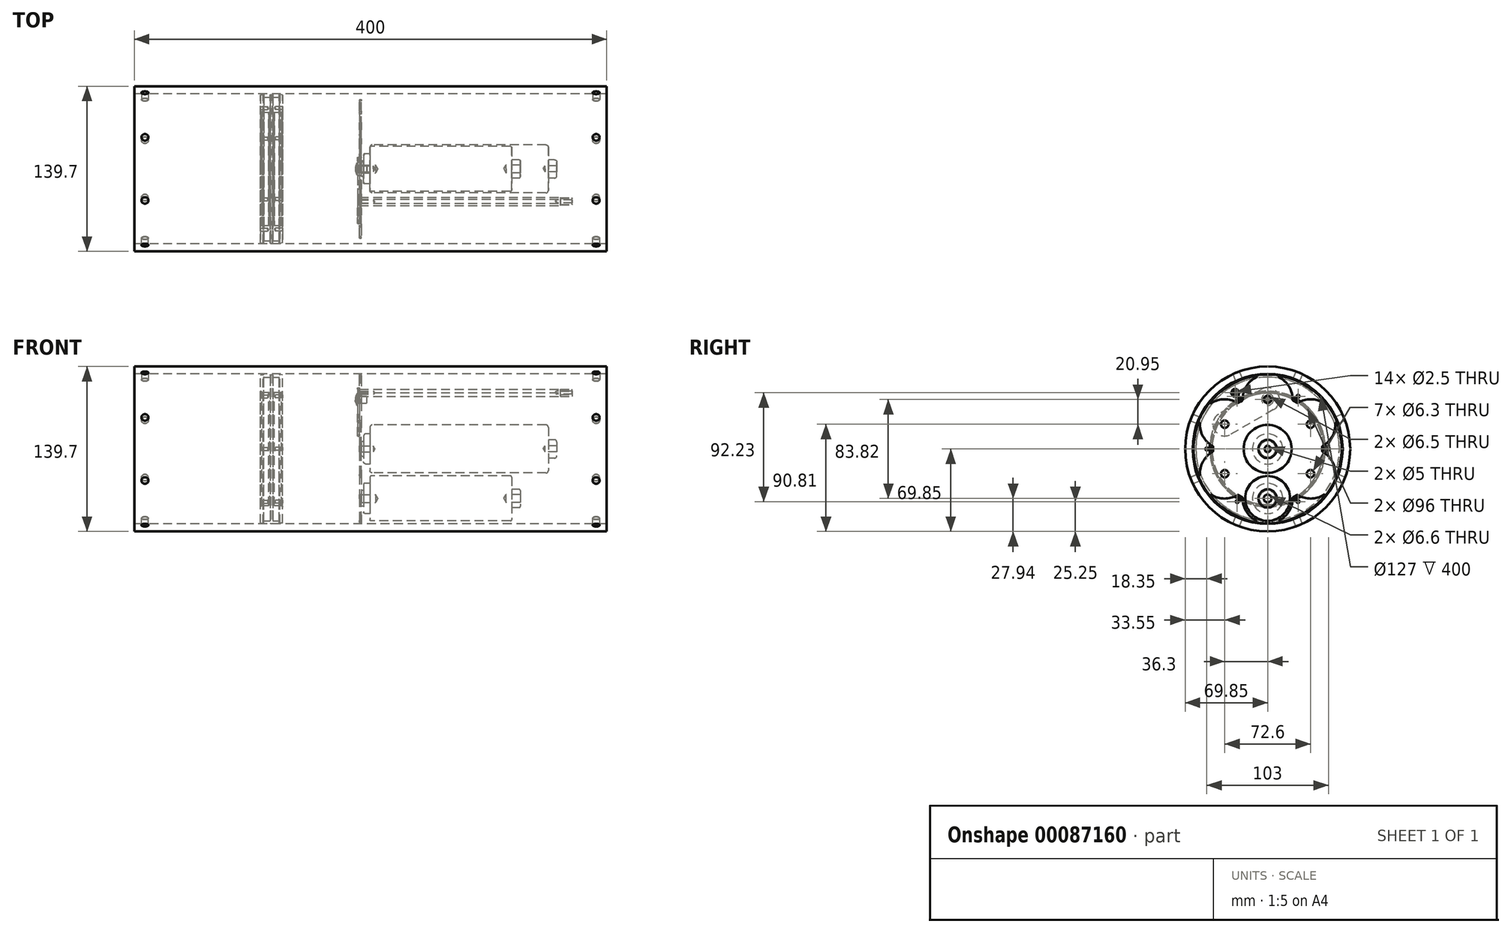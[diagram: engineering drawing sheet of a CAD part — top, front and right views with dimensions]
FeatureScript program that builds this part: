
annotation { "Feature Type Name" : "Feature", "Feature Type Description" : "" }
export const myFeature = defineFeature(function(context is Context, id is Id, definition is map)
    precondition{}
    {
        {
            var Q0;
            Q0=qCreatedBy(makeId("Front.planeOp"),FACE);
            var sketch = newSketch(context, id + "F0", { "sketchPlane" : qUnion([Q0])});
            skLineSegment(sketch, "E0", {"start": v(-82.75, 0) * mm, "end": v(82.75, 0) * mm});
            skLineSegment(sketch, "E1", {"start": v(-75.5, 20.32) * mm, "end": v(75.5, 20.32) * mm});
            skLineSegment(sketch, "E2", {"start": v(-82.75, 0) * mm, "end": v(-82.75, 6.75) * mm});
            skLineSegment(sketch, "E3", {"start": v(-82.75, 6.75) * mm, "end": v(-80.88, 6.75) * mm});
            skLineSegment(sketch, "E4", {"start": v(-80.88, 6.75) * mm, "end": v(-80.88, 12.8) * mm});
            skLineSegment(sketch, "E5", {"start": v(-80.88, 12.8) * mm, "end": v(-75.5, 12.8) * mm});
            skLineSegment(sketch, "E6", {"start": v(-75.5, 12.8) * mm, "end": v(-75.5, 20.32) * mm});
            skLineSegment(sketch, "E7", {"start": v(82.75, 0) * mm, "end": v(82.75, 7.75) * mm});
            skLineSegment(sketch, "E8", {"start": v(82.75, 7.75) * mm, "end": v(75.5, 7.75) * mm});
            skLineSegment(sketch, "E9", {"start": v(75.5, 7.75) * mm, "end": v(75.5, 20.32) * mm});
            skSolve(sketch);
        }
        {
            var Q0;
            Q0=makeQuery(id+"F0.imprint","IMPRINT",FACE,{"disambiguationData":[TD([[makeQuery(id+"F0.imprint","IMPRINT",EDGE,{"derivedFrom":sQuery(id+"F0.wireOp",EDGE,"E0")}),1.0]])]});
            var Q1;
            Q1=sQuery(id+"F0.wireOp",EDGE,"E0");
            revolve(context, id + "F1", {"entities" : qUnion([Q0]), "axis" : qUnion([Q1]), "revolveType" : RevolveType.FULL});
        }
        {
            var Q0;
            Q0=makeQuery(id+"F1.opRevolve","SWEPT_FACE",FACE,{"disambiguationData":[OSD([sQuery(id+"F0.wireOp",EDGE,"E1")])]});
            var Q1;
            Q1=makeQuery(id+"F1.opRevolve","SWEPT_EDGE",EDGE,{"disambiguationData":[OSD([sQuery(id+"F0.wireOp",EDGE,"E7"),sQuery(id+"F0.wireOp",EDGE,"E8")])]});
            var Q2;
            Q2=makeQuery(id+"F1.opRevolve","SWEPT_EDGE",EDGE,{"disambiguationData":[OSD([sQuery(id+"F0.wireOp",EDGE,"E4"),sQuery(id+"F0.wireOp",EDGE,"E5")])]});
            var Q3;
            Q3=makeQuery(id+"F1.opRevolve","SWEPT_EDGE",EDGE,{"disambiguationData":[OSD([sQuery(id+"F0.wireOp",EDGE,"E2"),sQuery(id+"F0.wireOp",EDGE,"E3")])]});
            fillet(context, id + "F2", {"entities" : qUnion([Q0, Q1, Q2, Q3]), "radius" : 2 * mm, "tangentPropagation" : true, "allowEdgeOverflow" : false});
        }
        {
            var Q0;
            Q0=makeQuery(id+"F1.opRevolve","SWEPT_FACE",FACE,{"disambiguationData":[OSD([sQuery(id+"F0.wireOp",EDGE,"E2")])]});
            var sketch = newSketch(context, id + "F3", { "sketchPlane" : qUnion([Q0])});
            skPoint(sketch, "E10", {"position": v(0, 0) * mm});
            skSolve(sketch);
        }
        {
            var Q0;
            Q0=makeQuery(id+"F1.opRevolve","SWEPT_FACE",FACE,{"disambiguationData":[OSD([sQuery(id+"F0.wireOp",EDGE,"E7")])]});
            var sketch = newSketch(context, id + "F4", { "sketchPlane" : qUnion([Q0])});
            skPoint(sketch, "E11", {"position": v(0, 0) * mm});
            skSolve(sketch);
        }
        {
            var Q0;
            Q0=sQuery(id+"F4.wireOp",VERTEX,"E11");
            var Q1;
            Q1=sQuery(id+"F3.wireOp",VERTEX,"E10");
            var Q2;
            Q2=makeQuery(id+"F1.opRevolve","SWEPT_BODY",BODY,{"disambiguationData":[OSD([sQuery(id+"F0.wireOp",EDGE,"E0"),sQuery(id+"F0.wireOp",EDGE,"E1"),sQuery(id+"F0.wireOp",EDGE,"E2"),sQuery(id+"F0.wireOp",EDGE,"E3"),sQuery(id+"F0.wireOp",EDGE,"E4"),sQuery(id+"F0.wireOp",EDGE,"E5"),sQuery(id+"F0.wireOp",EDGE,"E6"),sQuery(id+"F0.wireOp",EDGE,"E7"),sQuery(id+"F0.wireOp",EDGE,"E8"),sQuery(id+"F0.wireOp",EDGE,"E9")])]});
            hole(context, id + "F5", {"style" : HoleStyle.SIMPLE, "endStyle" : HoleEndStyle.BLIND, "standardTappedOrClearance" : lookupTablePath({ "standard" : "ISO", "engagement" : "75%", "pitch" : "1 mm", "size" : "M6", "type" : "Tapped" }), "standardBlindInLast" : lookupTablePath({ "standard" : "ISO", "engagement" : "75%", "pitch" : "1 mm", "size" : "M6", "type" : "Tapped" }), "holeDiameter" : 5 * mm, "holeDepth" : 10 * mm, "locations" : qUnion([Q0, Q1]), "scope" : qUnion([Q2]), "majorDiameter" : 6 * mm});
        }
        {
            var Q0;
            Q0=makeQuery(id+"F1.opRevolve","SWEPT_FACE",FACE,{"disambiguationData":[OSD([sQuery(id+"F0.wireOp",EDGE,"E2")])]});
            var sketch = newSketch(context, id + "F6", { "sketchPlane" : qUnion([Q0])});
            skCircle(sketch, "E12", {"center": v(0, 0) * mm, "radius": 63.5 * mm, "construction": true});
            skCircle(sketch, "E13.0", {"center": v(0, 0) * mm, "radius": 20.32 * mm, "construction": true});
            skLineSegment(sketch, "E14", {"start": v(0, 20.32) * mm, "end": v(0, 63.5) * mm, "construction": true});
            skCircle(sketch, "E15", {"center": v(0, 41.91) * mm, "radius": 20.32 * mm, "construction": true});
            skCircle(sketch, "E16", {"center": v(0, 41.91) * mm, "radius": 3.15 * mm});
            skCircle(sketch, "E17", {"center": v(0, 0) * mm, "radius": 3.15 * mm});
            skCircle(sketch, "E18", {"center": v(0, 0) * mm, "radius": 63 * mm});
            skCircle(sketch, "E19.1.0", {"center": v(-36.3, 20.96) * mm, "radius": 3.15 * mm});
            skCircle(sketch, "E19.2.0", {"center": v(-36.3, -20.96) * mm, "radius": 3.15 * mm});
            skCircle(sketch, "E19.3.0", {"center": v(0, -41.91) * mm, "radius": 3.15 * mm});
            skCircle(sketch, "E19.4.0", {"center": v(36.3, -20.96) * mm, "radius": 3.15 * mm});
            skCircle(sketch, "E19.5.0", {"center": v(36.3, 20.96) * mm, "radius": 3.15 * mm});
            skCircle(sketch, "E20", {"center": v(36.3, 20.96) * mm, "radius": 20.32 * mm, "construction": true});
            skCircle(sketch, "E21", {"center": v(0, 41.91) * mm, "radius": 10 * mm, "construction": true});
            skCircle(sketch, "E22", {"center": v(36.3, 20.96) * mm, "radius": 10 * mm, "construction": true});
            skLineSegment(sketch, "E23", {"start": v(-5, 33.25) * mm, "end": v(31.3, 12.3) * mm, "construction": true});
            skLineSegment(sketch, "E24", {"start": v(5, 50.57) * mm, "end": v(41.3, 29.62) * mm, "construction": true});
            skArc(sketch, "E25", {"start": v(0, 63) * mm, "mid": v(15.13, 56.6) * mm, "end": v(21.08, 41.29) * mm});
            skLineSegment(sketch, "E26", {"start": v(23.15, 40.1) * mm, "end": v(35.3, 61.15) * mm, "construction": true});
            skArc(sketch, "E27.MirrorCS", {"start": v(54.56, 31.5) * mm, "mid": v(41.45, 41.4) * mm, "end": v(25.22, 38.9) * mm});
            skLineSegment(sketch, "E28", {"start": v(21.08, 41.29) * mm, "end": v(25.22, 38.9) * mm});
            skLineSegment(sketch, "E29", {"start": v(9.66, 62.25) * mm, "end": v(9.43, 60.77) * mm});
            skCircle(sketch, "E30", {"center": v(0, -41.91) * mm, "radius": 19 * mm, "construction": true});
            skCircle(sketch, "E31", {"center": v(-36.3, -20.96) * mm, "radius": 19 * mm, "construction": true});
            skSolve(sketch);
        }
        {
            var Q0;
            Q0 = qSketchRegion(id + "F6", true);
            extrude(context, id + "F7", {"entities" : qUnion([Q0]), "depth" : 1.6 * mm});
        }
        {
            var Q0;
            Q0=makeQuery(id+"F7.opExtrude","CAP_FACE",FACE,{"disambiguationData":[OSD([sQuery(id+"F6.wireOp",EDGE,"E16"),sQuery(id+"F6.wireOp",EDGE,"E17"),sQuery(id+"F6.wireOp",EDGE,"E18"),sQuery(id+"F6.wireOp",EDGE,"E19.1.0"),sQuery(id+"F6.wireOp",EDGE,"E19.2.0"),sQuery(id+"F6.wireOp",EDGE,"E19.3.0"),sQuery(id+"F6.wireOp",EDGE,"E19.4.0"),sQuery(id+"F6.wireOp",EDGE,"E19.5.0")])],"isStart":false});
            var sketch = newSketch(context, id + "F8", { "sketchPlane" : qUnion([Q0])});
            skArc(sketch, "E32.0", {"start": v(9.94, 60.51) * mm, "mid": v(18.13, 52.69) * mm, "end": v(21.09, 41.75) * mm});
            skArc(sketch, "E32.1", {"start": v(47.44, 38.86) * mm, "mid": v(36.57, 42.04) * mm, "end": v(25.62, 39.14) * mm});
            skArc(sketch, "E32.2", {"start": v(49.08, 39.5) * mm, "mid": v(31.5, 54.56) * mm, "end": v(9.66, 62.25) * mm});
            skLineSegment(sketch, "E32.3", {"start": v(9.66, 62.25) * mm, "end": v(9.52, 61.34) * mm});
            skLineSegment(sketch, "E32.4", {"start": v(21.49, 41.05) * mm, "end": v(24.81, 39.14) * mm});
            skLineSegment(sketch, "E32.5", {"start": v(23.15, 40.1) * mm, "end": v(35.3, 61.15) * mm, "construction": true});
            skLineSegment(sketch, "E33.MirrorCS", {"start": v(49.08, 39.5) * mm, "end": v(48.36, 38.92) * mm});
            skPoint(sketch, "E34.orphan", {"position": v(54.56, 31.5) * mm});
            skPoint(sketch, "E35.orphan", {"position": v(0, 63) * mm});
            skPoint(sketch, "E36.visualSharp", {"position": v(21.08, 41.29) * mm});
            skArc(sketch, "E36.filletArc", {"start": v(21.09, 41.75) * mm, "mid": v(21.2, 41.35) * mm, "end": v(21.49, 41.05) * mm});
            skPoint(sketch, "E37.visualSharp", {"position": v(25.22, 38.9) * mm});
            skArc(sketch, "E37.filletArc", {"start": v(24.81, 39.14) * mm, "mid": v(25.21, 39.03) * mm, "end": v(25.62, 39.14) * mm});
            skPoint(sketch, "E38.visualSharp", {"position": v(47.91, 38.56) * mm});
            skArc(sketch, "E38.filletArc", {"start": v(47.44, 38.86) * mm, "mid": v(47.9, 38.74) * mm, "end": v(48.36, 38.92) * mm});
            skPoint(sketch, "E39.visualSharp", {"position": v(9.43, 60.77) * mm});
            skArc(sketch, "E39.filletArc", {"start": v(9.52, 61.34) * mm, "mid": v(9.6, 60.86) * mm, "end": v(9.94, 60.51) * mm});
            skPoint(sketch, "E40.1.1", {"position": v(-54.56, 31.5) * mm});
            skArc(sketch, "E40.1.2", {"start": v(-47.44, 38.86) * mm, "mid": v(-36.57, 42.04) * mm, "end": v(-25.62, 39.14) * mm});
            skArc(sketch, "E40.1.3", {"start": v(-9.94, 60.51) * mm, "mid": v(-18.13, 52.69) * mm, "end": v(-21.09, 41.75) * mm});
            skArc(sketch, "E40.1.4", {"start": v(-9.66, 62.25) * mm, "mid": v(-31.5, 54.56) * mm, "end": v(-49.08, 39.5) * mm});
            skLineSegment(sketch, "E40.1.5", {"start": v(-23.15, 40.1) * mm, "end": v(-35.3, 61.15) * mm, "construction": true});
            skPoint(sketch, "E40.1.6", {"position": v(-25.22, 38.9) * mm});
            skPoint(sketch, "E40.1.7", {"position": v(-21.08, 41.29) * mm});
            skPoint(sketch, "E40.1.8", {"position": v(-9.43, 60.77) * mm});
            skPoint(sketch, "E40.1.9", {"position": v(-47.91, 38.56) * mm});
            skLineSegment(sketch, "E40.1.10", {"start": v(-24.81, 39.14) * mm, "end": v(-21.49, 41.05) * mm});
            skArc(sketch, "E40.1.11", {"start": v(-48.36, 38.92) * mm, "mid": v(-47.9, 38.74) * mm, "end": v(-47.44, 38.86) * mm});
            skLineSegment(sketch, "E40.1.12", {"start": v(-49.08, 39.5) * mm, "end": v(-48.36, 38.92) * mm});
            skArc(sketch, "E40.1.13", {"start": v(-25.62, 39.14) * mm, "mid": v(-25.21, 39.03) * mm, "end": v(-24.81, 39.14) * mm});
            skArc(sketch, "E40.1.14", {"start": v(-21.49, 41.05) * mm, "mid": v(-21.2, 41.35) * mm, "end": v(-21.09, 41.75) * mm});
            skLineSegment(sketch, "E40.1.15", {"start": v(-9.66, 62.25) * mm, "end": v(-9.52, 61.34) * mm});
            skArc(sketch, "E40.1.16", {"start": v(-9.94, 60.51) * mm, "mid": v(-9.6, 60.86) * mm, "end": v(-9.52, 61.34) * mm});
            skPoint(sketch, "E40.2.0", {"position": v(-54.56, 31.5) * mm});
            skPoint(sketch, "E40.2.1", {"position": v(-54.56, -31.5) * mm});
            skArc(sketch, "E40.2.2", {"start": v(-57.37, -21.65) * mm, "mid": v(-54.7, -10.65) * mm, "end": v(-46.7, -2.61) * mm});
            skArc(sketch, "E40.2.3", {"start": v(-57.37, 21.65) * mm, "mid": v(-54.7, 10.65) * mm, "end": v(-46.7, 2.61) * mm});
            skArc(sketch, "E40.2.4", {"start": v(-58.75, 22.76) * mm, "mid": v(-63, 0) * mm, "end": v(-58.75, -22.76) * mm});
            skLineSegment(sketch, "E40.2.5", {"start": v(-46.3, 0) * mm, "end": v(-70.6, 0) * mm, "construction": true});
            skPoint(sketch, "E40.2.6", {"position": v(-46.3, -2.4) * mm});
            skPoint(sketch, "E40.2.7", {"position": v(-46.3, 2.4) * mm});
            skPoint(sketch, "E40.2.8", {"position": v(-57.35, 22.22) * mm});
            skPoint(sketch, "E40.2.9", {"position": v(-57.35, -22.22) * mm});
            skLineSegment(sketch, "E40.2.10", {"start": v(-46.3, -1.92) * mm, "end": v(-46.3, 1.92) * mm});
            skArc(sketch, "E40.2.11", {"start": v(-57.88, -22.42) * mm, "mid": v(-57.5, -22.12) * mm, "end": v(-57.37, -21.65) * mm});
            skLineSegment(sketch, "E40.2.12", {"start": v(-58.75, -22.76) * mm, "end": v(-57.88, -22.42) * mm});
            skArc(sketch, "E40.2.13", {"start": v(-46.7, -2.61) * mm, "mid": v(-46.4, -2.32) * mm, "end": v(-46.3, -1.92) * mm});
            skArc(sketch, "E40.2.14", {"start": v(-46.3, 1.92) * mm, "mid": v(-46.4, 2.32) * mm, "end": v(-46.7, 2.61) * mm});
            skLineSegment(sketch, "E40.2.15", {"start": v(-58.75, 22.76) * mm, "end": v(-57.88, 22.42) * mm});
            skArc(sketch, "E40.2.16", {"start": v(-57.37, 21.65) * mm, "mid": v(-57.5, 22.12) * mm, "end": v(-57.88, 22.42) * mm});
            skPoint(sketch, "E40.3.0", {"position": v(-54.56, -31.5) * mm});
            skPoint(sketch, "E40.3.1", {"position": v(0, -63) * mm});
            skArc(sketch, "E40.3.2", {"start": v(-9.94, -60.51) * mm, "mid": v(-18.13, -52.69) * mm, "end": v(-21.09, -41.75) * mm});
            skArc(sketch, "E40.3.3", {"start": v(-47.44, -38.86) * mm, "mid": v(-36.57, -42.04) * mm, "end": v(-25.62, -39.14) * mm});
            skArc(sketch, "E40.3.4", {"start": v(-49.08, -39.5) * mm, "mid": v(-31.5, -54.56) * mm, "end": v(-9.66, -62.25) * mm});
            skLineSegment(sketch, "E40.3.5", {"start": v(-23.15, -40.1) * mm, "end": v(-35.3, -61.15) * mm, "construction": true});
            skPoint(sketch, "E40.3.6", {"position": v(-21.08, -41.29) * mm});
            skPoint(sketch, "E40.3.7", {"position": v(-25.22, -38.9) * mm});
            skPoint(sketch, "E40.3.8", {"position": v(-47.91, -38.56) * mm});
            skPoint(sketch, "E40.3.9", {"position": v(-9.43, -60.77) * mm});
            skLineSegment(sketch, "E40.3.10", {"start": v(-21.49, -41.05) * mm, "end": v(-24.81, -39.14) * mm});
            skArc(sketch, "E40.3.11", {"start": v(-9.52, -61.34) * mm, "mid": v(-9.6, -60.86) * mm, "end": v(-9.94, -60.51) * mm});
            skLineSegment(sketch, "E40.3.12", {"start": v(-9.66, -62.25) * mm, "end": v(-9.52, -61.34) * mm});
            skArc(sketch, "E40.3.13", {"start": v(-21.09, -41.75) * mm, "mid": v(-21.2, -41.35) * mm, "end": v(-21.49, -41.05) * mm});
            skArc(sketch, "E40.3.14", {"start": v(-24.81, -39.14) * mm, "mid": v(-25.21, -39.03) * mm, "end": v(-25.62, -39.14) * mm});
            skLineSegment(sketch, "E40.3.15", {"start": v(-49.08, -39.5) * mm, "end": v(-48.36, -38.92) * mm});
            skArc(sketch, "E40.3.16", {"start": v(-47.44, -38.86) * mm, "mid": v(-47.9, -38.74) * mm, "end": v(-48.36, -38.92) * mm});
            skPoint(sketch, "E40.4.0", {"position": v(0, -63) * mm});
            skPoint(sketch, "E40.4.1", {"position": v(54.56, -31.5) * mm});
            skArc(sketch, "E40.4.2", {"start": v(47.44, -38.86) * mm, "mid": v(36.57, -42.04) * mm, "end": v(25.62, -39.14) * mm});
            skArc(sketch, "E40.4.3", {"start": v(9.94, -60.51) * mm, "mid": v(18.13, -52.69) * mm, "end": v(21.09, -41.75) * mm});
            skArc(sketch, "E40.4.4", {"start": v(9.66, -62.25) * mm, "mid": v(31.5, -54.56) * mm, "end": v(49.08, -39.5) * mm});
            skLineSegment(sketch, "E40.4.5", {"start": v(23.15, -40.1) * mm, "end": v(35.3, -61.15) * mm, "construction": true});
            skPoint(sketch, "E40.4.6", {"position": v(25.22, -38.9) * mm});
            skPoint(sketch, "E40.4.7", {"position": v(21.08, -41.29) * mm});
            skPoint(sketch, "E40.4.8", {"position": v(9.43, -60.77) * mm});
            skPoint(sketch, "E40.4.9", {"position": v(47.91, -38.56) * mm});
            skLineSegment(sketch, "E40.4.10", {"start": v(24.81, -39.14) * mm, "end": v(21.49, -41.05) * mm});
            skArc(sketch, "E40.4.11", {"start": v(48.36, -38.92) * mm, "mid": v(47.9, -38.74) * mm, "end": v(47.44, -38.86) * mm});
            skLineSegment(sketch, "E40.4.12", {"start": v(49.08, -39.5) * mm, "end": v(48.36, -38.92) * mm});
            skArc(sketch, "E40.4.13", {"start": v(25.62, -39.14) * mm, "mid": v(25.21, -39.03) * mm, "end": v(24.81, -39.14) * mm});
            skArc(sketch, "E40.4.14", {"start": v(21.49, -41.05) * mm, "mid": v(21.2, -41.35) * mm, "end": v(21.09, -41.75) * mm});
            skLineSegment(sketch, "E40.4.15", {"start": v(9.66, -62.25) * mm, "end": v(9.52, -61.34) * mm});
            skArc(sketch, "E40.4.16", {"start": v(9.94, -60.51) * mm, "mid": v(9.6, -60.86) * mm, "end": v(9.52, -61.34) * mm});
            skPoint(sketch, "E40.5.0", {"position": v(54.56, -31.5) * mm});
            skArc(sketch, "E40.5.2", {"start": v(57.37, 21.65) * mm, "mid": v(54.7, 10.65) * mm, "end": v(46.7, 2.61) * mm});
            skArc(sketch, "E40.5.3", {"start": v(57.37, -21.65) * mm, "mid": v(54.7, -10.65) * mm, "end": v(46.7, -2.61) * mm});
            skArc(sketch, "E40.5.4", {"start": v(58.75, -22.76) * mm, "mid": v(63, 0) * mm, "end": v(58.75, 22.76) * mm});
            skLineSegment(sketch, "E40.5.5", {"start": v(46.3, 0) * mm, "end": v(70.6, 0) * mm, "construction": true});
            skPoint(sketch, "E40.5.6", {"position": v(46.3, 2.4) * mm});
            skPoint(sketch, "E40.5.7", {"position": v(46.3, -2.4) * mm});
            skPoint(sketch, "E40.5.8", {"position": v(57.35, -22.22) * mm});
            skPoint(sketch, "E40.5.9", {"position": v(57.35, 22.22) * mm});
            skLineSegment(sketch, "E40.5.10", {"start": v(46.3, 1.92) * mm, "end": v(46.3, -1.92) * mm});
            skArc(sketch, "E40.5.11", {"start": v(57.88, 22.42) * mm, "mid": v(57.5, 22.12) * mm, "end": v(57.37, 21.65) * mm});
            skLineSegment(sketch, "E40.5.12", {"start": v(58.75, 22.76) * mm, "end": v(57.88, 22.42) * mm});
            skArc(sketch, "E40.5.13", {"start": v(46.7, 2.61) * mm, "mid": v(46.4, 2.32) * mm, "end": v(46.3, 1.92) * mm});
            skArc(sketch, "E40.5.14", {"start": v(46.3, -1.92) * mm, "mid": v(46.4, -2.32) * mm, "end": v(46.7, -2.61) * mm});
            skLineSegment(sketch, "E40.5.15", {"start": v(58.75, -22.76) * mm, "end": v(57.88, -22.42) * mm});
            skArc(sketch, "E40.5.16", {"start": v(57.37, -21.65) * mm, "mid": v(57.5, -22.12) * mm, "end": v(57.88, -22.42) * mm});
            skSolve(sketch);
        }
        {
            var Q0;
            Q0 = qSketchRegion(id + "F8", true);
            extrude(context, id + "F9", {"entities" : qUnion([Q0]), "operationType" : NewBodyOperationType.REMOVE, "oppositeDirection" : true, "depth" : 25 * mm});
        }
        {
            var Q0;
            Q0=makeQuery(id+"F9.boolean.opBoolean","COPY",EDGE,{"derivedFrom":makeQuery(id+"F9.opExtrude","SWEPT_EDGE",EDGE,{"disambiguationData":[OSD([sQuery(id+"F6.wireOp",EDGE,"E18"),sQuery(id+"F8.wireOp",EDGE,"E32.2"),sQuery(id+"F8.wireOp",EDGE,"E32.3")])]})});
            var Q1;
            Q1=makeQuery(id+"F9.boolean.opBoolean","COPY",EDGE,{"derivedFrom":makeQuery(id+"F9.opExtrude","SWEPT_EDGE",EDGE,{"disambiguationData":[OSD([sQuery(id+"F6.wireOp",EDGE,"E18"),sQuery(id+"F8.wireOp",EDGE,"E32.2"),sQuery(id+"F8.wireOp",EDGE,"E33.MirrorCS")])]})});
            var Q2;
            Q2=makeQuery(id+"FGbRxVnL68Y7Bjd_2.1.F9.boolean.opBoolean","COPY",EDGE,{"derivedFrom":makeQuery(id+"FGbRxVnL68Y7Bjd_2.1.F9.opExtrude","SWEPT_EDGE",EDGE,{"disambiguationData":[OSD([sQuery(id+"F6.wireOp",EDGE,"E18"),sQuery(id+"F8.wireOp",EDGE,"E32.2"),sQuery(id+"F8.wireOp",EDGE,"E32.3")])]})});
            var Q3;
            Q3=makeQuery(id+"FGbRxVnL68Y7Bjd_2.1.F9.boolean.opBoolean","COPY",EDGE,{"derivedFrom":makeQuery(id+"FGbRxVnL68Y7Bjd_2.1.F9.opExtrude","SWEPT_EDGE",EDGE,{"disambiguationData":[OSD([sQuery(id+"F6.wireOp",EDGE,"E18"),sQuery(id+"F8.wireOp",EDGE,"E32.2"),sQuery(id+"F8.wireOp",EDGE,"E33.MirrorCS")])]})});
            var Q4;
            Q4=makeQuery(id+"FGbRxVnL68Y7Bjd_2.2.F9.boolean.opBoolean","COPY",EDGE,{"derivedFrom":makeQuery(id+"FGbRxVnL68Y7Bjd_2.2.F9.opExtrude","SWEPT_EDGE",EDGE,{"disambiguationData":[OSD([sQuery(id+"F6.wireOp",EDGE,"E18"),sQuery(id+"F8.wireOp",EDGE,"E32.2"),sQuery(id+"F8.wireOp",EDGE,"E32.3")])]})});
            var Q5;
            Q5=makeQuery(id+"FGbRxVnL68Y7Bjd_2.2.F9.boolean.opBoolean","COPY",EDGE,{"derivedFrom":makeQuery(id+"FGbRxVnL68Y7Bjd_2.2.F9.opExtrude","SWEPT_EDGE",EDGE,{"disambiguationData":[OSD([sQuery(id+"F6.wireOp",EDGE,"E18"),sQuery(id+"F8.wireOp",EDGE,"E32.2"),sQuery(id+"F8.wireOp",EDGE,"E33.MirrorCS")])]})});
            var Q6;
            Q6=makeQuery(id+"FGbRxVnL68Y7Bjd_2.3.F9.boolean.opBoolean","COPY",EDGE,{"derivedFrom":makeQuery(id+"FGbRxVnL68Y7Bjd_2.3.F9.opExtrude","SWEPT_EDGE",EDGE,{"disambiguationData":[OSD([sQuery(id+"F6.wireOp",EDGE,"E18"),sQuery(id+"F8.wireOp",EDGE,"E32.2"),sQuery(id+"F8.wireOp",EDGE,"E32.3")])]})});
            var Q7;
            Q7=makeQuery(id+"FGbRxVnL68Y7Bjd_2.4.F9.boolean.opBoolean","COPY",EDGE,{"derivedFrom":makeQuery(id+"FGbRxVnL68Y7Bjd_2.4.F9.opExtrude","SWEPT_EDGE",EDGE,{"disambiguationData":[OSD([sQuery(id+"F6.wireOp",EDGE,"E18"),sQuery(id+"F8.wireOp",EDGE,"E32.2"),sQuery(id+"F8.wireOp",EDGE,"E32.3")])]})});
            var Q8;
            Q8=makeQuery(id+"FGbRxVnL68Y7Bjd_2.3.F9.boolean.opBoolean","COPY",EDGE,{"derivedFrom":makeQuery(id+"FGbRxVnL68Y7Bjd_2.3.F9.opExtrude","SWEPT_EDGE",EDGE,{"disambiguationData":[OSD([sQuery(id+"F6.wireOp",EDGE,"E18"),sQuery(id+"F8.wireOp",EDGE,"E32.2"),sQuery(id+"F8.wireOp",EDGE,"E33.MirrorCS")])]})});
            var Q9;
            Q9=makeQuery(id+"FGbRxVnL68Y7Bjd_2.4.F9.boolean.opBoolean","COPY",EDGE,{"derivedFrom":makeQuery(id+"FGbRxVnL68Y7Bjd_2.4.F9.opExtrude","SWEPT_EDGE",EDGE,{"disambiguationData":[OSD([sQuery(id+"F6.wireOp",EDGE,"E18"),sQuery(id+"F8.wireOp",EDGE,"E32.2"),sQuery(id+"F8.wireOp",EDGE,"E33.MirrorCS")])]})});
            var Q10;
            Q10=makeQuery(id+"FGbRxVnL68Y7Bjd_2.5.F9.boolean.opBoolean","COPY",EDGE,{"derivedFrom":makeQuery(id+"FGbRxVnL68Y7Bjd_2.5.F9.opExtrude","SWEPT_EDGE",EDGE,{"disambiguationData":[OSD([sQuery(id+"F6.wireOp",EDGE,"E18"),sQuery(id+"F8.wireOp",EDGE,"E32.2"),sQuery(id+"F8.wireOp",EDGE,"E32.3")])]})});
            var Q11;
            Q11=makeQuery(id+"FGbRxVnL68Y7Bjd_2.5.F9.boolean.opBoolean","COPY",EDGE,{"derivedFrom":makeQuery(id+"FGbRxVnL68Y7Bjd_2.5.F9.opExtrude","SWEPT_EDGE",EDGE,{"disambiguationData":[OSD([sQuery(id+"F6.wireOp",EDGE,"E18"),sQuery(id+"F8.wireOp",EDGE,"E32.2"),sQuery(id+"F8.wireOp",EDGE,"E33.MirrorCS")])]})});
            fillet(context, id + "F10", {"entities" : qUnion([Q0, Q1, Q2, Q3, Q4, Q5, Q6, Q7, Q8, Q9, Q10, Q11]), "radius" : .8 * mm, "tangentPropagation" : true, "allowEdgeOverflow" : false});
        }
        {
            var Q0;
            Q0=makeQuery(id+"F7.opExtrude","CAP_FACE",FACE,{"disambiguationData":[OSD([sQuery(id+"F6.wireOp",EDGE,"E16"),sQuery(id+"F6.wireOp",EDGE,"E17"),sQuery(id+"F6.wireOp",EDGE,"E18"),sQuery(id+"F6.wireOp",EDGE,"E19.1.0"),sQuery(id+"F6.wireOp",EDGE,"E19.2.0"),sQuery(id+"F6.wireOp",EDGE,"E19.3.0"),sQuery(id+"F6.wireOp",EDGE,"E19.4.0"),sQuery(id+"F6.wireOp",EDGE,"E19.5.0")])],"isStart":false});
            var sketch = newSketch(context, id + "F11", { "sketchPlane" : qUnion([Q0])});
            skLineSegment(sketch, "E41.0", {"start": v(-5, 33.25) * mm, "end": v(31.3, 12.3) * mm});
            skLineSegment(sketch, "E41.1", {"start": v(5, 50.57) * mm, "end": v(41.3, 29.62) * mm});
            skArc(sketch, "E41.2", {"start": v(5, 50.57) * mm, "mid": v(-8.66, 46.91) * mm, "end": v(-5, 33.25) * mm});
            skArc(sketch, "E41.3", {"start": v(31.3, 12.3) * mm, "mid": v(44.96, 15.96) * mm, "end": v(41.3, 29.62) * mm});
            skPoint(sketch, "E41.4", {"position": v(0, 41.91) * mm});
            skPoint(sketch, "E41.5", {"position": v(36.3, 20.96) * mm});
            skCircle(sketch, "E42", {"center": v(0, 41.91) * mm, "radius": 3.25 * mm});
            skCircle(sketch, "E43", {"center": v(36.3, 20.96) * mm, "radius": 3.25 * mm});
            skSolve(sketch);
        }
        {
            var Q0;
            Q0=makeQuery(id+"F11.imprint","IMPRINT",FACE,{"disambiguationData":[TD([[makeQuery(id+"F11.imprint","IMPRINT",EDGE,{"derivedFrom":sQuery(id+"F11.wireOp",EDGE,"E41.0")}),1.0]])]});
            extrude(context, id + "F12", {"entities" : qUnion([Q0]), "depth" : 1.6 * mm});
        }
        {
            var Q0;
            Q0=qCreatedBy(makeId("Front.planeOp"),FACE);
            var sketch = newSketch(context, id + "F13", { "sketchPlane" : qUnion([Q0])});
            skPoint(sketch, "E44.0", {"position": v(-82.75, 41.91) * mm});
            skLineSegment(sketch, "E45", {"start": v(-82.75, 41.91) * mm, "end": v(-64.6, 41.91) * mm});
            skLineSegment(sketch, "E46", {"start": v(-64.6, 41.91) * mm, "end": v(-82.75, 41.91) * mm});
            skLineSegment(sketch, "E47", {"start": v(-82.75, 41.91) * mm, "end": v(-93.65, 41.91) * mm});
            skLineSegment(sketch, "E48.0", {"start": v(-85.95, 50.57) * mm, "end": v(-85.95, 29.62) * mm, "construction": true});
            skLineSegment(sketch, "E49", {"start": v(-85.95, 46.91) * mm, "end": v(-86.45, 46.91) * mm});
            skLineSegment(sketch, "E50", {"start": v(-77.95, 41.91) * mm, "end": v(-77.95, 44.91) * mm});
            skLineSegment(sketch, "E51", {"start": v(-77.95, 44.91) * mm, "end": v(-85.95, 44.91) * mm});
            skLineSegment(sketch, "E52", {"start": v(-85.95, 44.91) * mm, "end": v(-85.95, 46.91) * mm});
            skArc(sketch, "E53", {"start": v(-86.45, 46.91) * mm, "mid": v(-87.57, 44.52) * mm, "end": v(-87.95, 41.91) * mm});
            skSolve(sketch);
        }
        {
            var Q0;
            Q0=makeQuery(id+"F13.imprint","IMPRINT",FACE,{"disambiguationData":[TD([[makeQuery(id+"F13.imprint","IMPRINT",EDGE,{"derivedFrom":sQuery(id+"F13.wireOp",EDGE,"E49")}),1.0]])]});
            var Q1;
            Q1=sQuery(id+"F13.wireOp",EDGE,"E46");
            revolve(context, id + "F14", {"entities" : qUnion([Q0]), "axis" : qUnion([Q1]), "revolveType" : RevolveType.FULL});
        }
        {
            var Q0;
            Q0=makeQuery(id+"F12.opExtrude","CAP_FACE",FACE,{"disambiguationData":[OSD([sQuery(id+"F11.wireOp",EDGE,"E41.0"),sQuery(id+"F11.wireOp",EDGE,"E41.1"),sQuery(id+"F11.wireOp",EDGE,"E41.2"),sQuery(id+"F11.wireOp",EDGE,"E41.3"),sQuery(id+"F11.wireOp",EDGE,"E42"),sQuery(id+"F11.wireOp",EDGE,"E43")])],"isStart":false});
            var sketch = newSketch(context, id + "F15", { "sketchPlane" : qUnion([Q0])});
            skLineSegment(sketch, "E54", {"start": v(0, 44.41) * mm, "end": v(0.5, 44.41) * mm});
            skLineSegment(sketch, "E55", {"start": v(0.5, 44.41) * mm, "end": v(0.5, 42.41) * mm});
            skLineSegment(sketch, "E56", {"start": v(0.5, 42.41) * mm, "end": v(2.5, 42.41) * mm});
            skLineSegment(sketch, "E57", {"start": v(2.5, 42.41) * mm, "end": v(2.5, 41.91) * mm});
            skLineSegment(sketch, "E58", {"start": v(2.5, 41.91) * mm, "end": v(0, 41.91) * mm});
            skLineSegment(sketch, "E59", {"start": v(0, 41.91) * mm, "end": v(0, 44.41) * mm, "construction": true});
            skLineSegment(sketch, "E60.1.0", {"start": v(-2.5, 41.91) * mm, "end": v(-2.5, 42.41) * mm});
            skLineSegment(sketch, "E60.1.1", {"start": v(-2.5, 42.41) * mm, "end": v(-0.5, 42.41) * mm});
            skLineSegment(sketch, "E60.1.2", {"start": v(-0.5, 42.41) * mm, "end": v(-0.5, 44.41) * mm});
            skLineSegment(sketch, "E60.1.3", {"start": v(-0.5, 44.41) * mm, "end": v(0, 44.41) * mm});
            skLineSegment(sketch, "E60.2.0", {"start": v(0, 39.41) * mm, "end": v(-0.5, 39.41) * mm});
            skLineSegment(sketch, "E60.2.1", {"start": v(-0.5, 39.41) * mm, "end": v(-0.5, 41.41) * mm});
            skLineSegment(sketch, "E60.2.2", {"start": v(-0.5, 41.41) * mm, "end": v(-2.5, 41.41) * mm});
            skLineSegment(sketch, "E60.2.3", {"start": v(-2.5, 41.41) * mm, "end": v(-2.5, 41.91) * mm});
            skLineSegment(sketch, "E60.3.0", {"start": v(2.5, 41.91) * mm, "end": v(2.5, 41.41) * mm});
            skLineSegment(sketch, "E60.3.1", {"start": v(2.5, 41.41) * mm, "end": v(0.5, 41.41) * mm});
            skLineSegment(sketch, "E60.3.2", {"start": v(0.5, 41.41) * mm, "end": v(0.5, 39.41) * mm});
            skLineSegment(sketch, "E60.3.3", {"start": v(0.5, 39.41) * mm, "end": v(0, 39.41) * mm});
            skPoint(sketch, "E60.center", {"position": v(0, 41.91) * mm});
            skSolve(sketch);
        }
        {
            var Q0;
            Q0 = qSketchRegion(id + "F15", true);
            extrude(context, id + "F16", {"entities" : qUnion([Q0]), "operationType" : NewBodyOperationType.REMOVE, "depth" : 25 * mm});
        }
        {
            var Q0;
            Q0=qCreatedBy(makeId("Right.planeOp"),FACE);
            var sketch = newSketch(context, id + "F17", { "sketchPlane" : qUnion([Q0])});
            skCircle(sketch, "E61", {"center": v(0, 0) * mm, "radius": 69.85 * mm});
            skCircle(sketch, "E62", {"center": v(0, 0) * mm, "radius": 63.5 * mm});
            skSolve(sketch);
        }
        {
            var Q0;
            Q0=makeQuery(id+"F17.imprint","IMPRINT",FACE,{"disambiguationData":[TD([[makeQuery(id+"F17.imprint","IMPRINT",EDGE,{"derivedFrom":sQuery(id+"F17.wireOp",EDGE,"E61")}),1.0]])]});
            var Q1;
            Q1 = qSketchRegion(id + "F20", true);
            extrude(context, id + "F18", {"entities" : qUnion([Q0, Q1]), "depth" : 125 * mm, "hasSecondDirection" : true, "secondDirectionOppositeDirection" : true, "secondDirectionDepth" : (400 - 125) * mm});
        }
        {
            var Q0;
            Q0=makeQuery(id+"F18.opExtrude","CAP_FACE",FACE,{"disambiguationData":[OSD([sQuery(id+"F17.wireOp",EDGE,"E61"),sQuery(id+"F17.wireOp",EDGE,"E62")])],"isStart":false});
            cPlane(context, id + "F19", {"entities" : qUnion([Q0]), "cplaneType" : CPlaneType.OFFSET, "offset" : 29.25 * mm + 3 / 406.4 * mm, "oppositeDirection" : true, "width" : 150 * mm, "height" : 150 * mm});
        }
        {
            var Q0;
            Q0=qCreatedBy(id+"F19.planeOp",FACE);
            var sketch = newSketch(context, id + "F20", { "sketchPlane" : qUnion([Q0])});
            skCircle(sketch, "E63", {"center": v(0, 0) * mm, "radius": 55 * mm, "construction": true});
            skCircle(sketch, "E64.cCircle", {"center": v(-27.5, 47.63) * mm, "radius": 3 * mm, "construction": true});
            skLineSegment(sketch, "E64.0", {"start": v(-29.23, 50.63) * mm, "end": v(-25.77, 50.63) * mm});
            skLineSegment(sketch, "E64.1", {"start": v(-25.77, 50.63) * mm, "end": v(-24.04, 47.63) * mm});
            skLineSegment(sketch, "E64.2", {"start": v(-24.04, 47.63) * mm, "end": v(-25.77, 44.63) * mm});
            skLineSegment(sketch, "E64.3", {"start": v(-25.77, 44.63) * mm, "end": v(-29.23, 44.63) * mm});
            skLineSegment(sketch, "E64.4", {"start": v(-29.23, 44.63) * mm, "end": v(-30.96, 47.63) * mm});
            skLineSegment(sketch, "E64.5", {"start": v(-30.96, 47.63) * mm, "end": v(-29.23, 50.63) * mm});
            skPoint(sketch, "E64.0.midPoint", {"position": v(-27.5, 50.63) * mm});
            skLineSegment(sketch, "E65", {"start": v(0, 0) * mm, "end": v(-27.5, 47.63) * mm, "construction": true});
            skLineSegment(sketch, "E66", {"start": v(0, 0) * mm, "end": v(0, 55) * mm, "construction": true});
            skSolve(sketch);
        }
        {
            var Q0;
            Q0 = qSketchRegion(id + "F20", true);
            extrude(context, id + "F21", {"entities" : qUnion([Q0]), "oppositeDirection" : true, "depth" : 180 * mm});
        }
        {
            var Q0;
            Q0=qCreatedBy(makeId("Front.planeOp"),FACE);
            var sketch = newSketch(context, id + "F22", { "sketchPlane" : qUnion([Q0])});
            skLineSegment(sketch, "E67", {"start": v(-82.75, -41.91) * mm, "end": v(51.75, -41.91) * mm});
            skLineSegment(sketch, "E68", {"start": v(-75.5, -22.91) * mm, "end": v(44.5, -22.91) * mm});
            skLineSegment(sketch, "E69", {"start": v(-82.75, -41.91) * mm, "end": v(-82.75, -35.16) * mm});
            skLineSegment(sketch, "E70", {"start": v(-82.75, -35.16) * mm, "end": v(-80.88, -35.16) * mm});
            skLineSegment(sketch, "E71", {"start": v(-80.88, -35.16) * mm, "end": v(-80.88, -29.11) * mm});
            skLineSegment(sketch, "E72", {"start": v(-80.88, -29.11) * mm, "end": v(-75.5, -29.11) * mm});
            skLineSegment(sketch, "E73", {"start": v(-75.5, -29.11) * mm, "end": v(-75.5, -22.91) * mm});
            skLineSegment(sketch, "E74", {"start": v(51.75, -41.91) * mm, "end": v(51.75, -34.16) * mm});
            skLineSegment(sketch, "E75", {"start": v(51.75, -34.16) * mm, "end": v(44.5, -34.16) * mm});
            skLineSegment(sketch, "E76", {"start": v(44.5, -34.16) * mm, "end": v(44.5, -22.91) * mm});
            skLineSegment(sketch, "E77.0", {"start": v(-82.75, -45.06) * mm, "end": v(-82.75, -38.76) * mm, "construction": true});
            skSolve(sketch);
        }
        {
            var Q0;
            Q0 = qSketchRegion(id + "F22", true);
            var Q1;
            Q1=sQuery(id+"F22.wireOp",EDGE,"E67");
            revolve(context, id + "F23", {"entities" : qUnion([Q0]), "axis" : qUnion([Q1]), "revolveType" : RevolveType.FULL});
        }
        {
            var Q0;
            Q0=makeQuery(id+"F23.opRevolve","SWEPT_EDGE",EDGE,{"disambiguationData":[OSD([sQuery(id+"F22.wireOp",EDGE,"E68"),sQuery(id+"F22.wireOp",EDGE,"E76")])]});
            var Q1;
            Q1=makeQuery(id+"F23.opRevolve","SWEPT_EDGE",EDGE,{"disambiguationData":[OSD([sQuery(id+"F22.wireOp",EDGE,"E74"),sQuery(id+"F22.wireOp",EDGE,"E75")])]});
            var Q2;
            Q2=makeQuery(id+"F23.opRevolve","SWEPT_EDGE",EDGE,{"disambiguationData":[OSD([sQuery(id+"F22.wireOp",EDGE,"E68"),sQuery(id+"F22.wireOp",EDGE,"E73")])]});
            var Q3;
            Q3=makeQuery(id+"F23.opRevolve","SWEPT_EDGE",EDGE,{"disambiguationData":[OSD([sQuery(id+"F22.wireOp",EDGE,"E71"),sQuery(id+"F22.wireOp",EDGE,"E72")])]});
            var Q4;
            Q4=makeQuery(id+"F23.opRevolve","SWEPT_EDGE",EDGE,{"disambiguationData":[OSD([sQuery(id+"F22.wireOp",EDGE,"E69"),sQuery(id+"F22.wireOp",EDGE,"E70")])]});
            fillet(context, id + "F24", {"entities" : qUnion([Q0, Q1, Q2, Q3, Q4]), "radius" : 1 * mm, "tangentPropagation" : true, "allowEdgeOverflow" : false});
        }
        {
            var Q0;
            Q0=makeQuery(id+"F23.opRevolve","SWEPT_FACE",FACE,{"disambiguationData":[OSD([sQuery(id+"F22.wireOp",EDGE,"E74")])]});
            var sketch = newSketch(context, id + "F25", { "sketchPlane" : qUnion([Q0])});
            skPoint(sketch, "E78", {"position": v(0, -41.91) * mm});
            skSolve(sketch);
        }
        {
            var Q0;
            Q0=makeQuery(id+"F23.opRevolve","SWEPT_FACE",FACE,{"disambiguationData":[OSD([sQuery(id+"F22.wireOp",EDGE,"E69")])]});
            var sketch = newSketch(context, id + "F26", { "sketchPlane" : qUnion([Q0])});
            skPoint(sketch, "E79", {"position": v(0, -41.91) * mm});
            skSolve(sketch);
        }
        {
            var Q0;
            Q0=sQuery(id+"F26.wireOp",VERTEX,"E79");
            var Q1;
            Q1=sQuery(id+"F25.wireOp",VERTEX,"E78");
            var Q2;
            Q2=makeQuery(id+"F23.opRevolve","SWEPT_BODY",BODY,{"disambiguationData":[OSD([sQuery(id+"F22.wireOp",EDGE,"E67"),sQuery(id+"F22.wireOp",EDGE,"E68"),sQuery(id+"F22.wireOp",EDGE,"E69"),sQuery(id+"F22.wireOp",EDGE,"E70"),sQuery(id+"F22.wireOp",EDGE,"E71"),sQuery(id+"F22.wireOp",EDGE,"E72"),sQuery(id+"F22.wireOp",EDGE,"E73"),sQuery(id+"F22.wireOp",EDGE,"E74"),sQuery(id+"F22.wireOp",EDGE,"E75"),sQuery(id+"F22.wireOp",EDGE,"E76")])]});
            hole(context, id + "F27", {"style" : HoleStyle.SIMPLE, "endStyle" : HoleEndStyle.BLIND, "standardTappedOrClearance" : lookupTablePath({ "standard" : "ISO", "fit" : "Normal", "size" : "M6", "type" : "Clearance" }), "standardBlindInLast" : lookupTablePath({ "fit" : "Standard", "standard" : "ISO", "size" : "M6", "type" : "Clearance" }), "holeDiameter" : 6.6 * mm, "holeDepth" : 12 * mm, "tappedDepth" : 12 * mm, "tapClearance" : 3, "locations" : qUnion([Q0, Q1]), "scope" : qUnion([Q2])});
        }
        {
            var Q0;
            Q0=makeQuery(id+"F21.opExtrude","CAP_FACE",FACE,{"disambiguationData":[OSD([sQuery(id+"F20.wireOp",EDGE,"E64.0"),sQuery(id+"F20.wireOp",EDGE,"E64.1"),sQuery(id+"F20.wireOp",EDGE,"E64.2"),sQuery(id+"F20.wireOp",EDGE,"E64.3"),sQuery(id+"F20.wireOp",EDGE,"E64.4"),sQuery(id+"F20.wireOp",EDGE,"E64.5")])],"isStart":true});
            var sketch = newSketch(context, id + "F28", { "sketchPlane" : qUnion([Q0])});
            skLineSegment(sketch, "E80.0.0", {"start": v(-29.23, 50.63) * mm, "end": v(-30.96, 47.63) * mm, "construction": true});
            skLineSegment(sketch, "E80.0.1", {"start": v(-30.96, 47.63) * mm, "end": v(-29.23, 44.63) * mm, "construction": true});
            skLineSegment(sketch, "E80.0.2", {"start": v(-29.23, 44.63) * mm, "end": v(-25.77, 44.63) * mm, "construction": true});
            skLineSegment(sketch, "E80.0.3", {"start": v(-25.77, 44.63) * mm, "end": v(-24.04, 47.63) * mm, "construction": true});
            skLineSegment(sketch, "E80.0.4", {"start": v(-24.04, 47.63) * mm, "end": v(-25.77, 50.63) * mm, "construction": true});
            skLineSegment(sketch, "E80.0.5", {"start": v(-25.77, 50.63) * mm, "end": v(-29.23, 50.63) * mm, "construction": true});
            skPoint(sketch, "E81", {"position": v(-27.5, 47.63) * mm});
            skPoint(sketch, "E81.positionSnap0", {"position": v(-27.5, 50.63) * mm});
            skSolve(sketch);
        }
        {
            var Q0;
            Q0=sQuery(id+"F28.wireOp",VERTEX,"E81");
            var Q1;
            Q1=makeQuery(id+"F21.opExtrude","SWEPT_BODY",BODY,{"disambiguationData":[OSD([sQuery(id+"F20.wireOp",EDGE,"E64.0"),sQuery(id+"F20.wireOp",EDGE,"E64.1"),sQuery(id+"F20.wireOp",EDGE,"E64.2"),sQuery(id+"F20.wireOp",EDGE,"E64.3"),sQuery(id+"F20.wireOp",EDGE,"E64.4"),sQuery(id+"F20.wireOp",EDGE,"E64.5")])]});
            hole(context, id + "F29", {"style" : HoleStyle.SIMPLE, "endStyle" : HoleEndStyle.BLIND, "standardTappedOrClearance" : lookupTablePath({ "standard" : "ISO", "engagement" : "75%", "pitch" : "0.5 mm", "size" : "M3", "type" : "Tapped" }), "standardBlindInLast" : lookupTablePath({ "standard" : "ISO", "engagement" : "75%", "pitch" : "0.5 mm", "size" : "M3", "type" : "Tapped" }), "holeDiameter" : 2.5 * mm, "showTappedDepth" : true, "holeDepth" : 13.5 * mm, "tappedDepth" : 12 * mm, "tapClearance" : 3, "locations" : qUnion([Q0]), "scope" : qUnion([Q1]), "majorDiameter" : 3 * mm});
        }
        {
            var Q0;
            Q0=makeQuery(id+"F21.opExtrude","CAP_FACE",FACE,{"disambiguationData":[OSD([sQuery(id+"F20.wireOp",EDGE,"E64.0"),sQuery(id+"F20.wireOp",EDGE,"E64.1"),sQuery(id+"F20.wireOp",EDGE,"E64.2"),sQuery(id+"F20.wireOp",EDGE,"E64.3"),sQuery(id+"F20.wireOp",EDGE,"E64.4"),sQuery(id+"F20.wireOp",EDGE,"E64.5")])],"isStart":true});
            var sketch = newSketch(context, id + "F30", { "sketchPlane" : qUnion([Q0])});
            skCircle(sketch, "E82", {"center": v(-27.5, 47.63) * mm, "radius": 3 * mm});
            skSolve(sketch);
        }
        {
            var Q0;
            Q0=makeQuery(id+"F30.imprint","IMPRINT",FACE,{"disambiguationData":[TD([[makeQuery(id+"F30.imprint","IMPRINT",EDGE,{"derivedFrom":sQuery(id+"F30.wireOp",EDGE,"E82")}),-1.0]])]});
            extrude(context, id + "F31", {"entities" : qUnion([Q0]), "operationType" : NewBodyOperationType.REMOVE, "oppositeDirection" : true, "depth" : 10 * mm});
        }
        {
            var Q0;
            Q0=qCreatedBy(makeId("Front.planeOp"),FACE);
            var sketch = newSketch(context, id + "F32", { "sketchPlane" : qUnion([Q0])});
            skLineSegment(sketch, "E83", {"start": v(-168.07, 63) * mm, "end": v(-149.57, 63) * mm, "construction": true});
            skLineSegment(sketch, "E84", {"start": v(0, 0) * mm, "end": v(-238.96, 0) * mm, "construction": true});
            skLineSegment(sketch, "E85", {"start": v(-158.82, 63) * mm, "end": v(-158.82, 0) * mm, "construction": true});
            skLineSegment(sketch, "E86", {"start": v(-158.82, 63) * mm, "end": v(-157.82, 63) * mm});
            skLineSegment(sketch, "E87", {"start": v(-157.82, 63) * mm, "end": v(-157.82, 60.83) * mm});
            skLineSegment(sketch, "E88", {"start": v(-157.82, 60.83) * mm, "end": v(-152.28, 60.83) * mm});
            skLineSegment(sketch, "E89", {"start": v(-152.28, 60.83) * mm, "end": v(-152.28, 63) * mm});
            skLineSegment(sketch, "E90", {"start": v(-152.28, 63) * mm, "end": v(-149.57, 63) * mm});
            skLineSegment(sketch, "E91.MirrorCS", {"start": v(-159.82, 63) * mm, "end": v(-159.82, 60.83) * mm});
            skLineSegment(sketch, "E92.MirrorCS", {"start": v(-159.82, 60.83) * mm, "end": v(-165.36, 60.83) * mm});
            skLineSegment(sketch, "E93.MirrorCS", {"start": v(-165.36, 60.83) * mm, "end": v(-165.36, 63) * mm});
            skLineSegment(sketch, "E94", {"start": v(-159.82, 63) * mm, "end": v(-158.82, 63) * mm});
            skLineSegment(sketch, "E95", {"start": v(-165.36, 63) * mm, "end": v(-168.07, 63) * mm});
            skLineSegment(sketch, "E96", {"start": v(-158.82, 0) * mm, "end": v(-157.32, 0) * mm});
            skLineSegment(sketch, "E97", {"start": v(-157.32, 0) * mm, "end": v(-157.32, 48) * mm});
            skLineSegment(sketch, "E98", {"start": v(-157.32, 48) * mm, "end": v(-149.57, 48) * mm});
            skLineSegment(sketch, "E99", {"start": v(-149.57, 48) * mm, "end": v(-149.57, 63) * mm});
            skLineSegment(sketch, "E100.MirrorCS", {"start": v(-160.32, 48) * mm, "end": v(-168.07, 48) * mm});
            skLineSegment(sketch, "E101.MirrorCS", {"start": v(-160.32, 0) * mm, "end": v(-160.32, 48) * mm});
            skLineSegment(sketch, "E102.MirrorCS", {"start": v(-168.07, 48) * mm, "end": v(-168.07, 63) * mm});
            skLineSegment(sketch, "E103", {"start": v(-160.32, 0) * mm, "end": v(-158.82, 0) * mm});
            skSolve(sketch);
        }
        {
            var Q0;
            Q0=makeQuery(id+"F32.imprint","IMPRINT",FACE,{"disambiguationData":[TD([[makeQuery(id+"F32.imprint","IMPRINT",EDGE,{"derivedFrom":sQuery(id+"F32.wireOp",EDGE,"E87")}),-1.0]])]});
            var Q1;
            Q1=sQuery(id+"F32.wireOp",EDGE,"E84");
            revolve(context, id + "F33", {"entities" : qUnion([Q0]), "axis" : qUnion([Q1]), "revolveType" : RevolveType.FULL});
        }
        {
            var Q0;
            Q0=makeQuery(id+"F33.opRevolve","SWEPT_EDGE",EDGE,{"disambiguationData":[OSD([sQuery(id+"F32.wireOp",EDGE,"E100.MirrorCS"),sQuery(id+"F32.wireOp",EDGE,"E102.MirrorCS")])]});
            var Q1;
            Q1=makeQuery(id+"F33.opRevolve","SWEPT_EDGE",EDGE,{"disambiguationData":[OSD([sQuery(id+"F32.wireOp",EDGE,"E98"),sQuery(id+"F32.wireOp",EDGE,"E99")])]});
            chamfer(context, id + "F34", {"entities" : qUnion([Q0, Q1]), "width" : 1 * mm, "tangentPropagation" : true});
        }
        {
            var Q0;
            Q0=makeQuery(id+"F33.opRevolve","SWEPT_EDGE",EDGE,{"disambiguationData":[OSD([sQuery(id+"F32.wireOp",EDGE,"E89"),sQuery(id+"F32.wireOp",EDGE,"E90")])]});
            var Q1;
            Q1=makeQuery(id+"F33.opRevolve","SWEPT_EDGE",EDGE,{"disambiguationData":[OSD([sQuery(id+"F32.wireOp",EDGE,"E87"),sQuery(id+"F32.wireOp",EDGE,"E86")])]});
            var Q2;
            Q2=makeQuery(id+"F33.opRevolve","SWEPT_EDGE",EDGE,{"disambiguationData":[OSD([sQuery(id+"F32.wireOp",EDGE,"E91.MirrorCS"),sQuery(id+"F32.wireOp",EDGE,"E94")])]});
            var Q3;
            Q3=makeQuery(id+"F33.opRevolve","SWEPT_EDGE",EDGE,{"disambiguationData":[OSD([sQuery(id+"F32.wireOp",EDGE,"E93.MirrorCS"),sQuery(id+"F32.wireOp",EDGE,"E95")])]});
            chamfer(context, id + "F35", {"entities" : qUnion([Q0, Q1, Q2, Q3]), "width" : .25 * mm, "tangentPropagation" : true});
        }
        {
            var Q0;
            Q0=makeQuery(id+"F33.opRevolve","SWEPT_FACE",FACE,{"disambiguationData":[OSD([sQuery(id+"F32.wireOp",EDGE,"E88")])]});
            var Q1;
            Q1=makeQuery(id+"F33.opRevolve","SWEPT_FACE",FACE,{"disambiguationData":[OSD([sQuery(id+"F32.wireOp",EDGE,"E92.MirrorCS")])]});
            fillet(context, id + "F36", {"entities" : qUnion([Q0, Q1]), "radius" : .2 * mm, "tangentPropagation" : true, "allowEdgeOverflow" : false});
        }
        {
            var Q0;
            Q0=makeQuery(id+"F33.opRevolve","SWEPT_EDGE",EDGE,{"disambiguationData":[OSD([sQuery(id+"F32.wireOp",EDGE,"E95"),sQuery(id+"F32.wireOp",EDGE,"E102.MirrorCS")])]});
            chamfer(context, id + "F37", {"entities" : qUnion([Q0]), "chamferType" : ChamferType.OFFSET_ANGLE, "width" : 2 * mm, "oppositeDirection" : false, "angle" : 10 * degree, "tangentPropagation" : true});
        }
        {
            var Q0;
            Q0=makeQuery(id+"F33.opRevolve","SWEPT_EDGE",EDGE,{"disambiguationData":[OSD([sQuery(id+"F32.wireOp",EDGE,"E90"),sQuery(id+"F32.wireOp",EDGE,"E99")])]});
            chamfer(context, id + "F38", {"entities" : qUnion([Q0]), "chamferType" : ChamferType.OFFSET_ANGLE, "width" : 2 * mm, "oppositeDirection" : true, "angle" : 10 * degree, "tangentPropagation" : true});
        }
        {
            var Q0;
            Q0=makeQuery(id+"F33.opRevolve","SWEPT_EDGE",EDGE,{"disambiguationData":[OSD([sQuery(id+"F32.wireOp",EDGE,"E100.MirrorCS"),sQuery(id+"F32.wireOp",EDGE,"E101.MirrorCS")])]});
            var Q1;
            Q1=makeQuery(id+"F33.opRevolve","SWEPT_EDGE",EDGE,{"disambiguationData":[OSD([sQuery(id+"F32.wireOp",EDGE,"E97"),sQuery(id+"F32.wireOp",EDGE,"E98")])]});
            chamfer(context, id + "F39", {"entities" : qUnion([Q0, Q1]), "width" : 1 * mm, "tangentPropagation" : true});
        }
        {
            var Q0;
            Q0=makeQuery(id+"F33.opRevolve","SWEPT_FACE",FACE,{"disambiguationData":[OSD([sQuery(id+"F32.wireOp",EDGE,"E102.MirrorCS")])]});
            var sketch = newSketch(context, id + "F40", { "sketchPlane" : qUnion([Q0])});
            skCircle(sketch, "E104.cCircle", {"center": v(0, 0) * mm, "radius": 51.5 * mm, "construction": true});
            skLineSegment(sketch, "E104.0", {"start": v(51.5, 0) * mm, "end": v(25.75, -44.6) * mm, "construction": true});
            skLineSegment(sketch, "E104.1", {"start": v(25.75, -44.6) * mm, "end": v(-25.75, -44.6) * mm, "construction": true});
            skLineSegment(sketch, "E104.2", {"start": v(-25.75, -44.6) * mm, "end": v(-51.5, 0) * mm, "construction": true});
            skLineSegment(sketch, "E104.3", {"start": v(-51.5, 0) * mm, "end": v(-25.75, 44.6) * mm, "construction": true});
            skLineSegment(sketch, "E104.4", {"start": v(-25.75, 44.6) * mm, "end": v(25.75, 44.6) * mm, "construction": true});
            skLineSegment(sketch, "E104.5", {"start": v(25.75, 44.6) * mm, "end": v(51.5, 0) * mm, "construction": true});
            skSolve(sketch);
        }
        {
            var Q0;
            Q0=makeQuery(id+"F33.opRevolve","SWEPT_FACE",FACE,{"disambiguationData":[OSD([sQuery(id+"F32.wireOp",EDGE,"E99")])]});
            var sketch = newSketch(context, id + "F41", { "sketchPlane" : qUnion([Q0])});
            skPoint(sketch, "E105.0", {"position": v(-25.75, 44.6) * mm});
            skPoint(sketch, "E105.1", {"position": v(-51.5, 0) * mm});
            skPoint(sketch, "E105.2", {"position": v(-25.75, -44.6) * mm});
            skPoint(sketch, "E105.3", {"position": v(25.75, -44.6) * mm});
            skPoint(sketch, "E105.4", {"position": v(51.5, 0) * mm});
            skPoint(sketch, "E105.5", {"position": v(25.75, 44.6) * mm});
            skSolve(sketch);
        }
        {
            var Q0;
            Q0=sQuery(id+"F40.wireOp",VERTEX,"E104.2.end");
            var Q1;
            Q1=sQuery(id+"F40.wireOp",VERTEX,"E104.4.start");
            var Q2;
            Q2=sQuery(id+"F40.wireOp",VERTEX,"E104.5.start");
            var Q3;
            Q3=sQuery(id+"F40.wireOp",VERTEX,"E104.0.start");
            var Q4;
            Q4=sQuery(id+"F40.wireOp",VERTEX,"E104.0.end");
            var Q5;
            Q5=sQuery(id+"F40.wireOp",VERTEX,"E104.1.end");
            var Q6;
            Q6=sQuery(id+"F41.wireOp",VERTEX,"E105.0");
            var Q7;
            Q7=sQuery(id+"F41.wireOp",VERTEX,"E105.1");
            var Q8;
            Q8=sQuery(id+"F41.wireOp",VERTEX,"E105.2");
            var Q9;
            Q9=sQuery(id+"F41.wireOp",VERTEX,"E105.3");
            var Q10;
            Q10=sQuery(id+"F41.wireOp",VERTEX,"E105.4");
            var Q11;
            Q11=sQuery(id+"F41.wireOp",VERTEX,"E105.5");
            var Q12;
            Q12=makeQuery(id+"F33.opRevolve","SWEPT_BODY",BODY,{"disambiguationData":[OSD([sQuery(id+"F32.wireOp",EDGE,"E87"),sQuery(id+"F32.wireOp",EDGE,"E88"),sQuery(id+"F32.wireOp",EDGE,"E89"),sQuery(id+"F32.wireOp",EDGE,"E86"),sQuery(id+"F32.wireOp",EDGE,"E90"),sQuery(id+"F32.wireOp",EDGE,"E91.MirrorCS"),sQuery(id+"F32.wireOp",EDGE,"E92.MirrorCS"),sQuery(id+"F32.wireOp",EDGE,"E93.MirrorCS"),sQuery(id+"F32.wireOp",EDGE,"E94"),sQuery(id+"F32.wireOp",EDGE,"E95"),sQuery(id+"F32.wireOp",EDGE,"E96"),sQuery(id+"F32.wireOp",EDGE,"E97"),sQuery(id+"F32.wireOp",EDGE,"E98"),sQuery(id+"F32.wireOp",EDGE,"E99"),sQuery(id+"F32.wireOp",EDGE,"E100.MirrorCS"),sQuery(id+"F32.wireOp",EDGE,"E101.MirrorCS"),sQuery(id+"F32.wireOp",EDGE,"E102.MirrorCS"),sQuery(id+"F32.wireOp",EDGE,"E103")])]});
            hole(context, id + "F42", {"style" : HoleStyle.SIMPLE, "endStyle" : HoleEndStyle.BLIND, "standardTappedOrClearance" : lookupTablePath({ "standard" : "ISO", "engagement" : "75%", "pitch" : "0.5 mm", "size" : "M3", "type" : "Tapped" }), "standardBlindInLast" : lookupTablePath({ "standard" : "ISO", "engagement" : "75%", "pitch" : "0.5 mm", "size" : "M3", "type" : "Tapped" }), "holeDiameter" : 2.5 * mm, "showTappedDepth" : true, "holeDepth" : 6 * mm, "tappedDepth" : 5 * mm, "tapClearance" : 2, "locations" : qUnion([Q0, Q1, Q2, Q3, Q4, Q5, Q6, Q7, Q8, Q9, Q10, Q11]), "scope" : qUnion([Q12]), "majorDiameter" : 3 * mm});
        }
        {
            var Q0;
            Q0=makeQuery(id+"F21.opExtrude","CAP_FACE",FACE,{"disambiguationData":[OSD([sQuery(id+"F20.wireOp",EDGE,"E64.0"),sQuery(id+"F20.wireOp",EDGE,"E64.1"),sQuery(id+"F20.wireOp",EDGE,"E64.2"),sQuery(id+"F20.wireOp",EDGE,"E64.3"),sQuery(id+"F20.wireOp",EDGE,"E64.4"),sQuery(id+"F20.wireOp",EDGE,"E64.5")])],"isStart":false});
            var sketch = newSketch(context, id + "F43", { "sketchPlane" : qUnion([Q0])});
            skPoint(sketch, "E106", {"position": v(27.5, 47.63) * mm});
            skPoint(sketch, "E106.positionSnap0", {"position": v(27.5, 50.63) * mm});
            skSolve(sketch);
        }
        {
            var Q0;
            Q0=sQuery(id+"F43.wireOp",VERTEX,"E106");
            var Q1;
            Q1=makeQuery(id+"F21.opExtrude","SWEPT_BODY",BODY,{"disambiguationData":[OSD([sQuery(id+"F20.wireOp",EDGE,"E64.0"),sQuery(id+"F20.wireOp",EDGE,"E64.1"),sQuery(id+"F20.wireOp",EDGE,"E64.2"),sQuery(id+"F20.wireOp",EDGE,"E64.3"),sQuery(id+"F20.wireOp",EDGE,"E64.4"),sQuery(id+"F20.wireOp",EDGE,"E64.5")])]});
            hole(context, id + "F44", {"style" : HoleStyle.SIMPLE, "endStyle" : HoleEndStyle.BLIND, "standardTappedOrClearance" : lookupTablePath({ "standard" : "ISO", "engagement" : "75%", "pitch" : "0.5 mm", "size" : "M3", "type" : "Tapped" }), "standardBlindInLast" : lookupTablePath({ "standard" : "ISO", "engagement" : "75%", "pitch" : "0.5 mm", "size" : "M3", "type" : "Tapped" }), "holeDiameter" : 2.5 * mm, "showTappedDepth" : true, "holeDepth" : 12 * mm, "tappedDepth" : 11 * mm, "tapClearance" : 2, "locations" : qUnion([Q0]), "scope" : qUnion([Q1]), "majorDiameter" : 3 * mm});
        }
        {
            var Q0;
            Q0=makeQuery(id+"F18.opExtrude","CAP_FACE",FACE,{"disambiguationData":[OSD([sQuery(id+"F17.wireOp",EDGE,"E61"),sQuery(id+"F17.wireOp",EDGE,"E62")])],"isStart":true});
            cPlane(context, id + "F45", {"entities" : qUnion([Q0]), "cplaneType" : CPlaneType.OFFSET, "offset" : 9 * mm, "oppositeDirection" : true, "width" : 150 * mm, "height" : 150 * mm});
        }
        {
            var Q0;
            Q0=makeQuery(id+"F18.opExtrude","CAP_FACE",FACE,{"disambiguationData":[OSD([sQuery(id+"F17.wireOp",EDGE,"E61"),sQuery(id+"F17.wireOp",EDGE,"E62")])],"isStart":false});
            cPlane(context, id + "F46", {"entities" : qUnion([Q0]), "cplaneType" : CPlaneType.OFFSET, "offset" : 9 * mm, "oppositeDirection" : true, "width" : 150 * mm, "height" : 150 * mm});
        }
        {
            var Q0;
            Q0=qCreatedBy(id+"F45.planeOp",FACE);
            var sketch = newSketch(context, id + "F47", { "sketchPlane" : qUnion([Q0])});
            skCircle(sketch, "E107.0", {"center": v(0, 0) * mm, "radius": 69.85 * mm, "construction": true});
            skLineSegment(sketch, "E108", {"start": v(0, 0) * mm, "end": v(26.73, 64.53) * mm, "construction": true});
            skLineSegment(sketch, "E109", {"start": v(0, 0) * mm, "end": v(0, 69.85) * mm});
            skLineSegment(sketch, "E110.1.0", {"start": v(0, 0) * mm, "end": v(-26.73, 64.53) * mm, "construction": true});
            skLineSegment(sketch, "E110.2.0", {"start": v(0, 0) * mm, "end": v(-64.53, 26.73) * mm, "construction": true});
            skLineSegment(sketch, "E110.3.0", {"start": v(0, 0) * mm, "end": v(-64.53, -26.73) * mm, "construction": true});
            skLineSegment(sketch, "E110.4.0", {"start": v(0, 0) * mm, "end": v(-26.73, -64.53) * mm, "construction": true});
            skLineSegment(sketch, "E110.5.0", {"start": v(0, 0) * mm, "end": v(26.73, -64.53) * mm, "construction": true});
            skLineSegment(sketch, "E110.6.0", {"start": v(0, 0) * mm, "end": v(64.53, -26.73) * mm, "construction": true});
            skLineSegment(sketch, "E110.7.0", {"start": v(0, 0) * mm, "end": v(64.53, 26.73) * mm, "construction": true});
            skSolve(sketch);
        }
        {
            var Q0;
            Q0=qCreatedBy(id+"F46.planeOp",FACE);
            var sketch = newSketch(context, id + "F48", { "sketchPlane" : qUnion([Q0])});
            skPoint(sketch, "E111.0", {"position": v(0, 0) * mm});
            skSolve(sketch);
        }
        {
            var Q0;
            Q0=sQuery(id+"F47.wireOp",EDGE,"E108");
            var Q1;
            Q1=sQuery(id+"F47.wireOp",VERTEX,"E108.end");
            cPlane(context, id + "F49", {"entities" : qUnion([Q0, Q1]), "cplaneType" : CPlaneType.LINE_POINT, "offset" : 25 * mm, "width" : 150 * mm, "height" : 150 * mm});
        }
        {
            var Q0;
            Q0=sQuery(id+"F47.wireOp",EDGE,"E110.7.0");
            var Q1;
            Q1=sQuery(id+"F47.wireOp",VERTEX,"E110.7.0.end");
            cPlane(context, id + "F50", {"entities" : qUnion([Q0, Q1]), "cplaneType" : CPlaneType.LINE_POINT, "offset" : 25 * mm, "width" : 150 * mm, "height" : 150 * mm});
        }
        {
            var Q0;
            Q0=sQuery(id+"F47.wireOp",EDGE,"E110.6.0");
            var Q1;
            Q1=sQuery(id+"F47.wireOp",VERTEX,"E110.6.0.end");
            cPlane(context, id + "F51", {"entities" : qUnion([Q0, Q1]), "cplaneType" : CPlaneType.LINE_POINT, "offset" : 25 * mm, "width" : 150 * mm, "height" : 150 * mm});
        }
        {
            var Q0;
            Q0=sQuery(id+"F47.wireOp",EDGE,"E110.5.0");
            var Q1;
            Q1=sQuery(id+"F47.wireOp",VERTEX,"E110.5.0.end");
            cPlane(context, id + "F52", {"entities" : qUnion([Q0, Q1]), "cplaneType" : CPlaneType.LINE_POINT, "offset" : 25 * mm, "width" : 150 * mm, "height" : 150 * mm});
        }
        {
            var Q0;
            Q0=sQuery(id+"F47.wireOp",EDGE,"E110.4.0");
            var Q1;
            Q1=sQuery(id+"F47.wireOp",VERTEX,"E110.4.0.end");
            cPlane(context, id + "F53", {"entities" : qUnion([Q0, Q1]), "cplaneType" : CPlaneType.LINE_POINT, "offset" : 25 * mm, "width" : 150 * mm, "height" : 150 * mm});
        }
        {
            var Q0;
            Q0=sQuery(id+"F47.wireOp",EDGE,"E110.3.0");
            var Q1;
            Q1=sQuery(id+"F47.wireOp",VERTEX,"E110.3.0.end");
            cPlane(context, id + "F54", {"entities" : qUnion([Q0, Q1]), "cplaneType" : CPlaneType.LINE_POINT, "offset" : 25 * mm, "width" : 150 * mm, "height" : 150 * mm});
        }
        {
            var Q0;
            Q0=sQuery(id+"F47.wireOp",EDGE,"E110.2.0");
            var Q1;
            Q1=sQuery(id+"F47.wireOp",VERTEX,"E110.2.0.end");
            cPlane(context, id + "F55", {"entities" : qUnion([Q0, Q1]), "cplaneType" : CPlaneType.LINE_POINT, "offset" : 25 * mm, "width" : 150 * mm, "height" : 150 * mm});
        }
        {
            var Q0;
            Q0=sQuery(id+"F47.wireOp",EDGE,"E110.1.0");
            var Q1;
            Q1=sQuery(id+"F47.wireOp",VERTEX,"E110.1.0.end");
            cPlane(context, id + "F56", {"entities" : qUnion([Q0, Q1]), "cplaneType" : CPlaneType.LINE_POINT, "offset" : 25 * mm, "width" : 150 * mm, "height" : 150 * mm});
        }
        {
            var Q0;
            Q0=qCreatedBy(id+"F50.planeOp",FACE);
            var sketch = newSketch(context, id + "F57", { "sketchPlane" : qUnion([Q0])});
            skPoint(sketch, "E112.0", {"position": v(-266, 0) * mm});
            skPoint(sketch, "E113.0", {"position": v(116, 0) * mm});
            skSolve(sketch);
        }
        {
            var Q0;
            Q0=qCreatedBy(id+"F49.planeOp",FACE);
            var sketch = newSketch(context, id + "F58", { "sketchPlane" : qUnion([Q0])});
            skPoint(sketch, "E114.0", {"position": v(-266, 0) * mm});
            skPoint(sketch, "E114.1", {"position": v(116, 0) * mm});
            skSolve(sketch);
        }
        {
            var Q0;
            Q0=qCreatedBy(id+"F51.planeOp",FACE);
            var sketch = newSketch(context, id + "F59", { "sketchPlane" : qUnion([Q0])});
            skPoint(sketch, "E115.0", {"position": v(-266, 0) * mm});
            skPoint(sketch, "E115.1", {"position": v(116, 0) * mm});
            skSolve(sketch);
        }
        {
            var Q0;
            Q0=qCreatedBy(id+"F52.planeOp",FACE);
            var sketch = newSketch(context, id + "F60", { "sketchPlane" : qUnion([Q0])});
            skPoint(sketch, "E116.0", {"position": v(-266, 0) * mm});
            skPoint(sketch, "E116.1", {"position": v(116, 0) * mm});
            skSolve(sketch);
        }
        {
            var Q0;
            Q0=qCreatedBy(id+"F53.planeOp",FACE);
            var sketch = newSketch(context, id + "F61", { "sketchPlane" : qUnion([Q0])});
            skPoint(sketch, "E117.0", {"position": v(-266, 0) * mm});
            skPoint(sketch, "E117.1", {"position": v(116, 0) * mm});
            skSolve(sketch);
        }
        {
            var Q0;
            Q0=qCreatedBy(id+"F54.planeOp",FACE);
            var sketch = newSketch(context, id + "F62", { "sketchPlane" : qUnion([Q0])});
            skPoint(sketch, "E118.0", {"position": v(266, 0) * mm});
            skPoint(sketch, "E118.1", {"position": v(-116, 0) * mm});
            skSolve(sketch);
        }
        {
            var Q0;
            Q0=qCreatedBy(id+"F55.planeOp",FACE);
            var sketch = newSketch(context, id + "F63", { "sketchPlane" : qUnion([Q0])});
            skPoint(sketch, "E119.0", {"position": v(266, 0) * mm});
            skPoint(sketch, "E119.1", {"position": v(-116, 0) * mm});
            skSolve(sketch);
        }
        {
            var Q0;
            Q0=qCreatedBy(id+"F56.planeOp",FACE);
            var sketch = newSketch(context, id + "F64", { "sketchPlane" : qUnion([Q0])});
            skPoint(sketch, "E120.0", {"position": v(-266, 0) * mm});
            skPoint(sketch, "E120.1", {"position": v(116, 0) * mm});
            skSolve(sketch);
        }
        {
            var Q0;
            Q0=sQuery(id+"F58.wireOp",VERTEX,"E114.0");
            var Q1;
            Q1=sQuery(id+"F64.wireOp",VERTEX,"E120.0");
            var Q2;
            Q2=sQuery(id+"F63.wireOp",VERTEX,"E119.0");
            var Q3;
            Q3=sQuery(id+"F62.wireOp",VERTEX,"E118.0");
            var Q4;
            Q4=sQuery(id+"F61.wireOp",VERTEX,"E117.0");
            var Q5;
            Q5=sQuery(id+"F60.wireOp",VERTEX,"E116.0");
            var Q6;
            Q6=sQuery(id+"F59.wireOp",VERTEX,"E115.0");
            var Q7;
            Q7=sQuery(id+"F57.wireOp",VERTEX,"E112.0");
            var Q8;
            Q8=sQuery(id+"F61.wireOp",VERTEX,"E117.1");
            var Q9;
            Q9=sQuery(id+"F60.wireOp",VERTEX,"E116.1");
            var Q10;
            Q10=sQuery(id+"F59.wireOp",VERTEX,"E115.1");
            var Q11;
            Q11=sQuery(id+"F57.wireOp",VERTEX,"E113.0");
            var Q12;
            Q12=sQuery(id+"F58.wireOp",VERTEX,"E114.1");
            var Q13;
            Q13=sQuery(id+"F64.wireOp",VERTEX,"E120.1");
            var Q14;
            Q14=sQuery(id+"F63.wireOp",VERTEX,"E119.1");
            var Q15;
            Q15=sQuery(id+"F62.wireOp",VERTEX,"E118.1");
            var Q16;
            Q16=makeQuery(id+"F18.opExtrude","SWEPT_BODY",BODY,{"disambiguationData":[OSD([sQuery(id+"F17.wireOp",EDGE,"E61"),sQuery(id+"F17.wireOp",EDGE,"E62")])]});
            hole(context, id + "F65", {"style" : HoleStyle.SIMPLE, "endStyle" : HoleEndStyle.BLIND, "holeDiameter" : 6 * mm, "holeDepth" : 12 * mm, "tappedDepth" : 12 * mm, "tapClearance" : 3, "locations" : qUnion([Q0, Q1, Q2, Q3, Q4, Q5, Q6, Q7, Q8, Q9, Q10, Q11, Q12, Q13, Q14, Q15]), "scope" : qUnion([Q16])});
        }
    });
